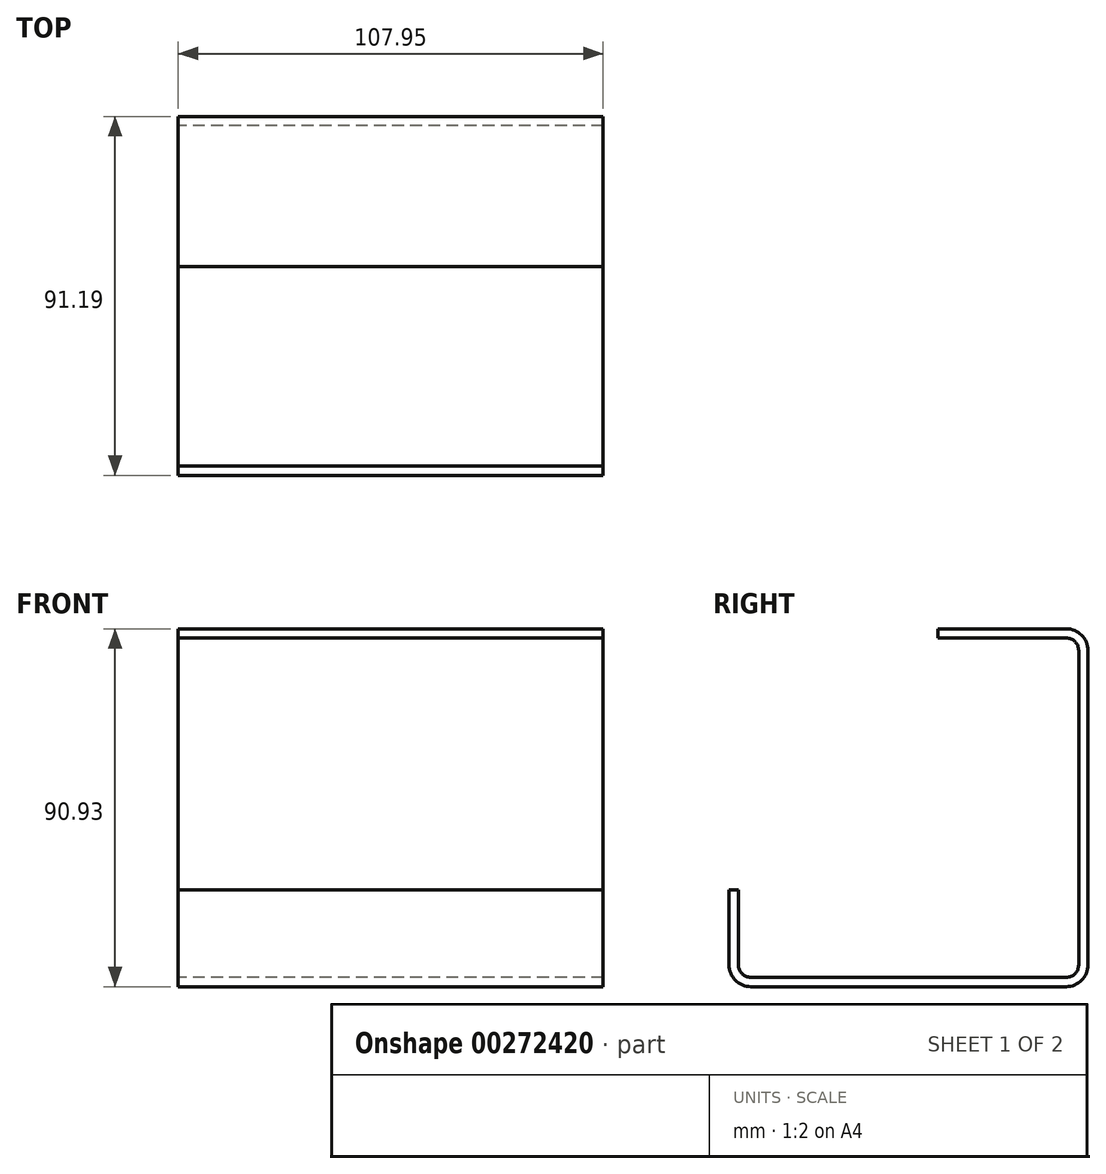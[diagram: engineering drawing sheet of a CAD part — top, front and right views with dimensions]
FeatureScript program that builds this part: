
annotation { "Feature Type Name" : "Feature", "Feature Type Description" : "" }
export const myFeature = defineFeature(function(context is Context, id is Id, definition is map)
    precondition{}
    {
        {
            var Q0;
            Q0=qCreatedBy(makeId("Right.planeOp"),FACE);
            var sketch = newSketch(context, id + "F0", { "sketchPlane" : qUnion([Q0])});
            skLineSegment(sketch, "E0", {"start": v(-91.19, 24.64) * mm, "end": v(-91.19, 5.54) * mm});
            skLineSegment(sketch, "E1", {"start": v(-85.65, 0) * mm, "end": v(-5.54, 0) * mm});
            skLineSegment(sketch, "E2", {"start": v(0, 5.54) * mm, "end": v(0, 85.4) * mm});
            skLineSegment(sketch, "E3", {"start": v(-5.54, 90.93) * mm, "end": v(-38.1, 90.93) * mm});
            skLineSegment(sketch, "E4.0", {"start": v(-5.54, 88.57) * mm, "end": v(-38.1, 88.57) * mm});
            skLineSegment(sketch, "E4.1", {"start": v(-2.36, 5.54) * mm, "end": v(-2.36, 85.4) * mm});
            skLineSegment(sketch, "E4.2", {"start": v(-85.65, 2.36) * mm, "end": v(-5.54, 2.36) * mm});
            skLineSegment(sketch, "E4.3", {"start": v(-88.82, 24.64) * mm, "end": v(-88.82, 5.54) * mm});
            skPoint(sketch, "E5.visualSharp", {"position": v(-88.82, 2.36) * mm});
            skArc(sketch, "E5.filletArc", {"start": v(-88.82, 5.54) * mm, "mid": v(-87.9, 3.3) * mm, "end": v(-85.65, 2.36) * mm});
            skPoint(sketch, "E6.visualSharp", {"position": v(-91.19, 0) * mm});
            skPoint(sketch, "E7.visualSharp", {"position": v(-2.36, 2.36) * mm});
            skArc(sketch, "E7.filletArc", {"start": v(-5.54, 2.36) * mm, "mid": v(-3.3, 3.3) * mm, "end": v(-2.36, 5.54) * mm});
            skPoint(sketch, "E8.visualSharp", {"position": v(-2.36, 88.57) * mm});
            skArc(sketch, "E8.filletArc", {"start": v(-2.36, 85.4) * mm, "mid": v(-3.3, 87.64) * mm, "end": v(-5.54, 88.57) * mm});
            skArc(sketch, "E9.0", {"start": v(-91.19, 5.54) * mm, "mid": v(-89.56, 1.62) * mm, "end": v(-85.65, 0) * mm});
            skArc(sketch, "E10.0", {"start": v(-5.54, 0) * mm, "mid": v(-1.62, 1.62) * mm, "end": v(0, 5.54) * mm});
            skArc(sketch, "E11.0", {"start": v(0, 85.4) * mm, "mid": v(-1.62, 89.31) * mm, "end": v(-5.54, 90.93) * mm});
            skPoint(sketch, "E12.orphan", {"position": v(0, 0) * mm});
            skLineSegment(sketch, "E13", {"start": v(-91.19, 24.64) * mm, "end": v(-88.82, 24.64) * mm});
            skLineSegment(sketch, "E14", {"start": v(-38.1, 90.93) * mm, "end": v(-38.1, 88.57) * mm});
            skSolve(sketch);
        }
        {
            var Q0;
            Q0=makeQuery(id+"F0.imprint","IMPRINT",FACE,{"disambiguationData":[TD([[makeQuery(id+"F0.imprint","IMPRINT",EDGE,{"derivedFrom":sQuery(id+"F0.wireOp",EDGE,"E0")}),1.0]])]});
            extrude(context, id + "F1", {"entities" : qUnion([Q0]), "depth" : 107.95 * mm});
        }
    });
